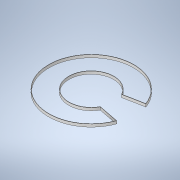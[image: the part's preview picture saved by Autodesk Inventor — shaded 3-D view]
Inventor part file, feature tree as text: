
AUTODESK INVENTOR PART (.ipt)
format: ipt  version: 2020 (Build 240168000, 168)  size: 127,488 bytes
history: native  units: mm
features: extrude x1, sketch x1
ambient origin geometry x8: Origin, YZ Plane, XZ Plane, XY Plane, X Axis, Y Axis, Z Axis, Center Point
bodies: Solid1 (feature_tree)
feature tree (2):
  extrude  "Extrusion1"  Depth=30.0mm
  sketch  "Sketch1"  dims[d0=504.787567mm d1=944.787567mm d41=4.0mm d42=4.0mm d43=4.0mm d44=4.0mm d45=30.0mm d46=0.0mm]
